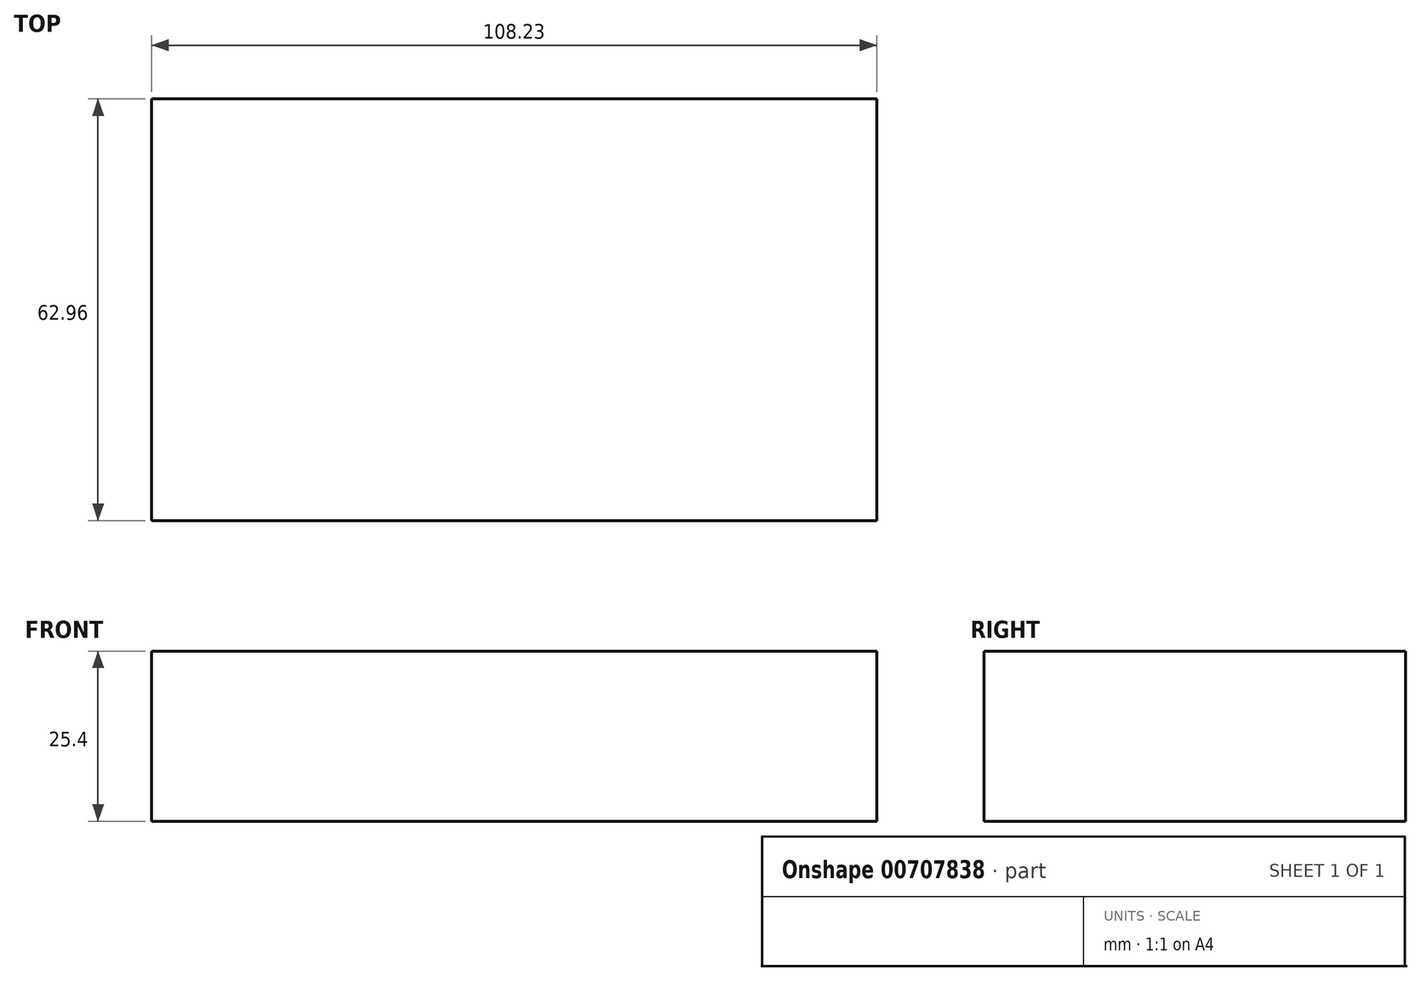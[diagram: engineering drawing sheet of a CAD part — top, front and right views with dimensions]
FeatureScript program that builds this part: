
annotation { "Feature Type Name" : "Feature", "Feature Type Description" : "" }
export const myFeature = defineFeature(function(context is Context, id is Id, definition is map)
    precondition{}
    {
        {
            var Q0;
            Q0=qCreatedBy(makeId("Top.planeOp"),FACE);
            var sketch = newSketch(context, id + "F0", { "sketchPlane" : qUnion([Q0])});
            skLineSegment(sketch, "E0.bottom", {"start": v(-80.3, 0) * mm, "end": v(27.93, 0) * mm});
            skLineSegment(sketch, "E0.top", {"start": v(-80.3, -62.96) * mm, "end": v(27.93, -62.96) * mm});
            skLineSegment(sketch, "E0.left", {"start": v(-80.3, 0) * mm, "end": v(-80.3, -62.96) * mm});
            skLineSegment(sketch, "E0.right", {"start": v(27.93, 0) * mm, "end": v(27.93, -62.96) * mm});
            skSolve(sketch);
        }
        {
            var Q0;
            Q0 = qSketchRegion(id + "F0", true);
            extrude(context, id + "F1", {"entities" : qUnion([Q0]), "depth" : 25.4 * mm, "offsetDistance" : 25.4 * mm});
        }
    });
